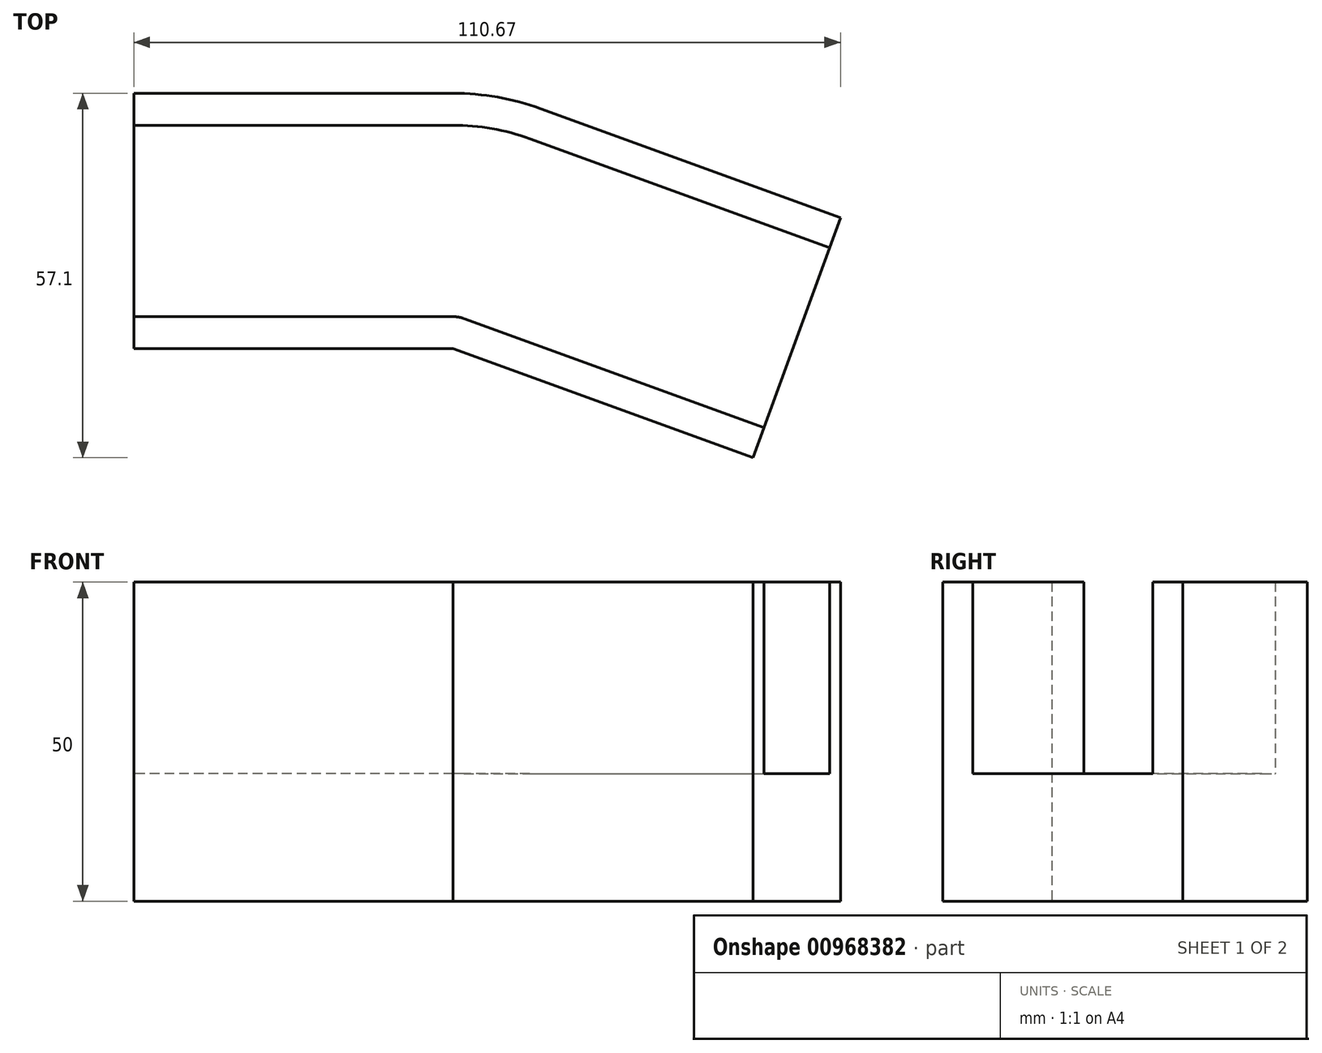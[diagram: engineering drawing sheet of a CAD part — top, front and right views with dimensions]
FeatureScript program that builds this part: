
annotation { "Feature Type Name" : "Feature", "Feature Type Description" : "" }
export const myFeature = defineFeature(function(context is Context, id is Id, definition is map)
    precondition{}
    {
        {
            var Q0;
            Q0=qCreatedBy(makeId("Top.planeOp"),FACE);
            var sketch = newSketch(context, id + "F0", { "sketchPlane" : qUnion([Q0])});
            skLineSegment(sketch, "E0.bottom", {"start": v(-50, 0) * mm, "end": v(0, 0) * mm});
            skLineSegment(sketch, "E0.top", {"start": v(-50, 40) * mm, "end": v(0, 40) * mm});
            skLineSegment(sketch, "E0.left", {"start": v(-50, 0) * mm, "end": v(-50, 40) * mm});
            skLineSegment(sketch, "E0.right", {"start": v(0, 0) * mm, "end": v(0, 40) * mm});
            skLineSegment(sketch, "E1.0", {"start": v(-50, 35) * mm, "end": v(0, 35) * mm});
            skLineSegment(sketch, "E2.0", {"start": v(-50, 5) * mm, "end": v(0, 5) * mm});
            skLineSegment(sketch, "E3", {"start": v(0, 0) * mm, "end": v(10.42, 59.1) * mm});
            skLineSegment(sketch, "E4.MirrorCS", {"start": v(60.67, 20.49) * mm, "end": v(13.68, 37.59) * mm});
            skLineSegment(sketch, "E5.MirrorCS", {"start": v(0, 0) * mm, "end": v(13.68, 37.59) * mm});
            skLineSegment(sketch, "E6.MirrorCS", {"start": v(58.96, 15.79) * mm, "end": v(11.97, 32.89) * mm});
            skLineSegment(sketch, "E7.MirrorCS", {"start": v(48.7, -12.4) * mm, "end": v(1.71, 4.7) * mm});
            skLineSegment(sketch, "E8.MirrorCS", {"start": v(46.98, -17.1) * mm, "end": v(0, 0) * mm});
            skLineSegment(sketch, "E9.MirrorCS", {"start": v(46.98, -17.1) * mm, "end": v(60.67, 20.49) * mm});
            skArc(sketch, "E10", {"start": v(13.68, 37.59) * mm, "mid": v(6.95, 39.4) * mm, "end": v(0, 40) * mm});
            skArc(sketch, "E11", {"start": v(11.97, 32.89) * mm, "mid": v(6.08, 34.47) * mm, "end": v(0, 35) * mm});
            skArc(sketch, "E12", {"start": v(1.71, 4.7) * mm, "mid": v(0.87, 4.92) * mm, "end": v(0, 5) * mm});
            skSolve(sketch);
        }
        {
            var Q0;
            {var subQ0=sQuery(id+"F0.wireOp",EDGE,"E1.0");Q0=makeQuery(id+"F0.imprint","IMPRINT",FACE,{"disambiguationData":[TD([[makeQuery(id+"F0.imprint","IMPRINT",EDGE,{"derivedFrom":subQ0}),-1.0]])]});}
            var Q1;
            {var subQ0=sQuery(id+"F0.wireOp",EDGE,"E0.top");Q1=makeQuery(id+"F0.imprint","IMPRINT",FACE,{"disambiguationData":[TD([[makeQuery(id+"F0.imprint","IMPRINT",EDGE,{"derivedFrom":subQ0}),-1.0]])]});}
            var Q2;
            {var subQ0=sQuery(id+"F0.wireOp",EDGE,"E0.bottom");Q2=makeQuery(id+"F0.imprint","IMPRINT",FACE,{"disambiguationData":[TD([[makeQuery(id+"F0.imprint","IMPRINT",EDGE,{"derivedFrom":subQ0}),1.0]])]});}
            var Q3;
            {var subQ3=sQuery(id+"F0.wireOp",EDGE,"E12");var subQ5=sQuery(id+"F0.wireOp",EDGE,"E3");var subQ6=makeQuery(id+"F0.imprint","INTERSECT",VERTEX,{"derivedFrom":[subQ5,subQ3]});Q3=makeQuery(id+"F0.imprint","IMPRINT",FACE,{"disambiguationData":[TD([[makeQuery(id+"F0.imprint","IMPRINT",EDGE,{"disambiguationData":[TD([[subQ6,-1.0]])],"derivedFrom":subQ5}),1.0]])]});}
            var Q4;
            {var subQ0=sQuery(id+"F0.wireOp",EDGE,"E12");var subQ1=sQuery(id+"F0.wireOp",EDGE,"E3");var subQ2=makeQuery(id+"F0.imprint","INTERSECT",VERTEX,{"derivedFrom":[subQ1,subQ0]});Q4=makeQuery(id+"F0.imprint","IMPRINT",FACE,{"disambiguationData":[TD([[makeQuery(id+"F0.imprint","IMPRINT",EDGE,{"disambiguationData":[TD([[subQ2,-1.0]])],"derivedFrom":subQ1}),-1.0]])]});}
            var Q5;
            {var subQ0=sQuery(id+"F0.wireOp",EDGE,"E10");var subQ1=sQuery(id+"F0.wireOp",EDGE,"E3");var subQ2=makeQuery(id+"F0.imprint","INTERSECT",VERTEX,{"derivedFrom":[subQ1,subQ0]});Q5=makeQuery(id+"F0.imprint","IMPRINT",FACE,{"disambiguationData":[TD([[makeQuery(id+"F0.imprint","IMPRINT",EDGE,{"disambiguationData":[TD([[subQ2,1.0]])],"derivedFrom":subQ1}),-1.0]])]});}
            var Q6;
            {var subQ0=sQuery(id+"F0.wireOp",EDGE,"E10");var subQ5=sQuery(id+"F0.wireOp",EDGE,"E3");var subQ6=makeQuery(id+"F0.imprint","INTERSECT",VERTEX,{"derivedFrom":[subQ5,subQ0]});Q6=makeQuery(id+"F0.imprint","IMPRINT",FACE,{"disambiguationData":[TD([[makeQuery(id+"F0.imprint","IMPRINT",EDGE,{"disambiguationData":[TD([[subQ6,1.0]])],"derivedFrom":subQ5}),1.0]])]});}
            var Q7;
            {var subQ0=sQuery(id+"F0.wireOp",EDGE,"E3");var subQ3=sQuery(id+"F0.wireOp",EDGE,"E12");var subQ5=makeQuery(id+"F0.imprint","INTERSECT",VERTEX,{"derivedFrom":[subQ0,subQ3]});Q7=makeQuery(id+"F0.imprint","IMPRINT",FACE,{"disambiguationData":[TD([[makeQuery(id+"F0.imprint","IMPRINT",EDGE,{"disambiguationData":[TD([[subQ5,-1.0]])],"derivedFrom":subQ3}),1.0]])]});}
            var Q8;
            {var subQ1=sQuery(id+"F0.wireOp",EDGE,"E3");var subQ3=sQuery(id+"F0.wireOp",EDGE,"E12");var subQ4=makeQuery(id+"F0.imprint","INTERSECT",VERTEX,{"derivedFrom":[subQ1,subQ3]});Q8=makeQuery(id+"F0.imprint","IMPRINT",FACE,{"disambiguationData":[TD([[makeQuery(id+"F0.imprint","IMPRINT",EDGE,{"disambiguationData":[TD([[subQ4,1.0]])],"derivedFrom":subQ3}),1.0]])]});}
            var Q9;
            {var subQ2=sQuery(id+"F0.wireOp",EDGE,"E7.MirrorCS");Q9=makeQuery(id+"F0.imprint","IMPRINT",FACE,{"disambiguationData":[TD([[makeQuery(id+"F0.imprint","IMPRINT",EDGE,{"derivedFrom":subQ2}),1.0]])]});}
            var Q10;
            {var subQ0=sQuery(id+"F0.wireOp",EDGE,"E6.MirrorCS");Q10=makeQuery(id+"F0.imprint","IMPRINT",FACE,{"disambiguationData":[TD([[makeQuery(id+"F0.imprint","IMPRINT",EDGE,{"derivedFrom":subQ0}),1.0]])]});}
            var Q11;
            {var subQ0=sQuery(id+"F0.wireOp",EDGE,"E4.MirrorCS");Q11=makeQuery(id+"F0.imprint","IMPRINT",FACE,{"disambiguationData":[TD([[makeQuery(id+"F0.imprint","IMPRINT",EDGE,{"derivedFrom":subQ0}),1.0]])]});}
            extrude(context, id + "F1", {"entities" : qUnion([Q0, Q1, Q2, Q3, Q4, Q5, Q6, Q7, Q8, Q9, Q10, Q11]), "depth" : 20 * mm, "offsetDistance" : 25 * mm});
        }
        {
            var Q0;
            {var subQ0=sQuery(id+"F0.wireOp",EDGE,"E10");var subQ1=sQuery(id+"F0.wireOp",EDGE,"E3");var subQ2=makeQuery(id+"F0.imprint","INTERSECT",VERTEX,{"derivedFrom":[subQ1,subQ0]});Q0=makeQuery(id+"F0.imprint","IMPRINT",FACE,{"disambiguationData":[TD([[makeQuery(id+"F0.imprint","IMPRINT",EDGE,{"disambiguationData":[TD([[subQ2,1.0]])],"derivedFrom":subQ1}),-1.0]])]});}
            var Q1;
            {var subQ0=sQuery(id+"F0.wireOp",EDGE,"E4.MirrorCS");Q1=makeQuery(id+"F0.imprint","IMPRINT",FACE,{"disambiguationData":[TD([[makeQuery(id+"F0.imprint","IMPRINT",EDGE,{"derivedFrom":subQ0}),1.0]])]});}
            var Q2;
            {var subQ0=sQuery(id+"F0.wireOp",EDGE,"E10");var subQ5=sQuery(id+"F0.wireOp",EDGE,"E3");var subQ6=makeQuery(id+"F0.imprint","INTERSECT",VERTEX,{"derivedFrom":[subQ5,subQ0]});Q2=makeQuery(id+"F0.imprint","IMPRINT",FACE,{"disambiguationData":[TD([[makeQuery(id+"F0.imprint","IMPRINT",EDGE,{"disambiguationData":[TD([[subQ6,1.0]])],"derivedFrom":subQ5}),1.0]])]});}
            var Q3;
            {var subQ0=sQuery(id+"F0.wireOp",EDGE,"E0.top");Q3=makeQuery(id+"F0.imprint","IMPRINT",FACE,{"disambiguationData":[TD([[makeQuery(id+"F0.imprint","IMPRINT",EDGE,{"derivedFrom":subQ0}),-1.0]])]});}
            var Q4;
            {var subQ2=sQuery(id+"F0.wireOp",EDGE,"E7.MirrorCS");Q4=makeQuery(id+"F0.imprint","IMPRINT",FACE,{"disambiguationData":[TD([[makeQuery(id+"F0.imprint","IMPRINT",EDGE,{"derivedFrom":subQ2}),1.0]])]});}
            var Q5;
            {var subQ0=sQuery(id+"F0.wireOp",EDGE,"E0.bottom");Q5=makeQuery(id+"F0.imprint","IMPRINT",FACE,{"disambiguationData":[TD([[makeQuery(id+"F0.imprint","IMPRINT",EDGE,{"derivedFrom":subQ0}),1.0]])]});}
            var Q6;
            {var subQ0=sQuery(id+"F0.wireOp",EDGE,"E3");var subQ3=sQuery(id+"F0.wireOp",EDGE,"E12");var subQ5=makeQuery(id+"F0.imprint","INTERSECT",VERTEX,{"derivedFrom":[subQ0,subQ3]});Q6=makeQuery(id+"F0.imprint","IMPRINT",FACE,{"disambiguationData":[TD([[makeQuery(id+"F0.imprint","IMPRINT",EDGE,{"disambiguationData":[TD([[subQ5,-1.0]])],"derivedFrom":subQ3}),1.0]])]});}
            var Q7;
            {var subQ1=sQuery(id+"F0.wireOp",EDGE,"E3");var subQ3=sQuery(id+"F0.wireOp",EDGE,"E12");var subQ4=makeQuery(id+"F0.imprint","INTERSECT",VERTEX,{"derivedFrom":[subQ1,subQ3]});Q7=makeQuery(id+"F0.imprint","IMPRINT",FACE,{"disambiguationData":[TD([[makeQuery(id+"F0.imprint","IMPRINT",EDGE,{"disambiguationData":[TD([[subQ4,1.0]])],"derivedFrom":subQ3}),1.0]])]});}
            extrude(context, id + "F2", {"entities" : qUnion([Q0, Q1, Q2, Q3, Q4, Q5, Q6, Q7]), "operationType" : NewBodyOperationType.ADD, "depth" : 50 * mm, "offsetDistance" : 25 * mm});
        }
    });
